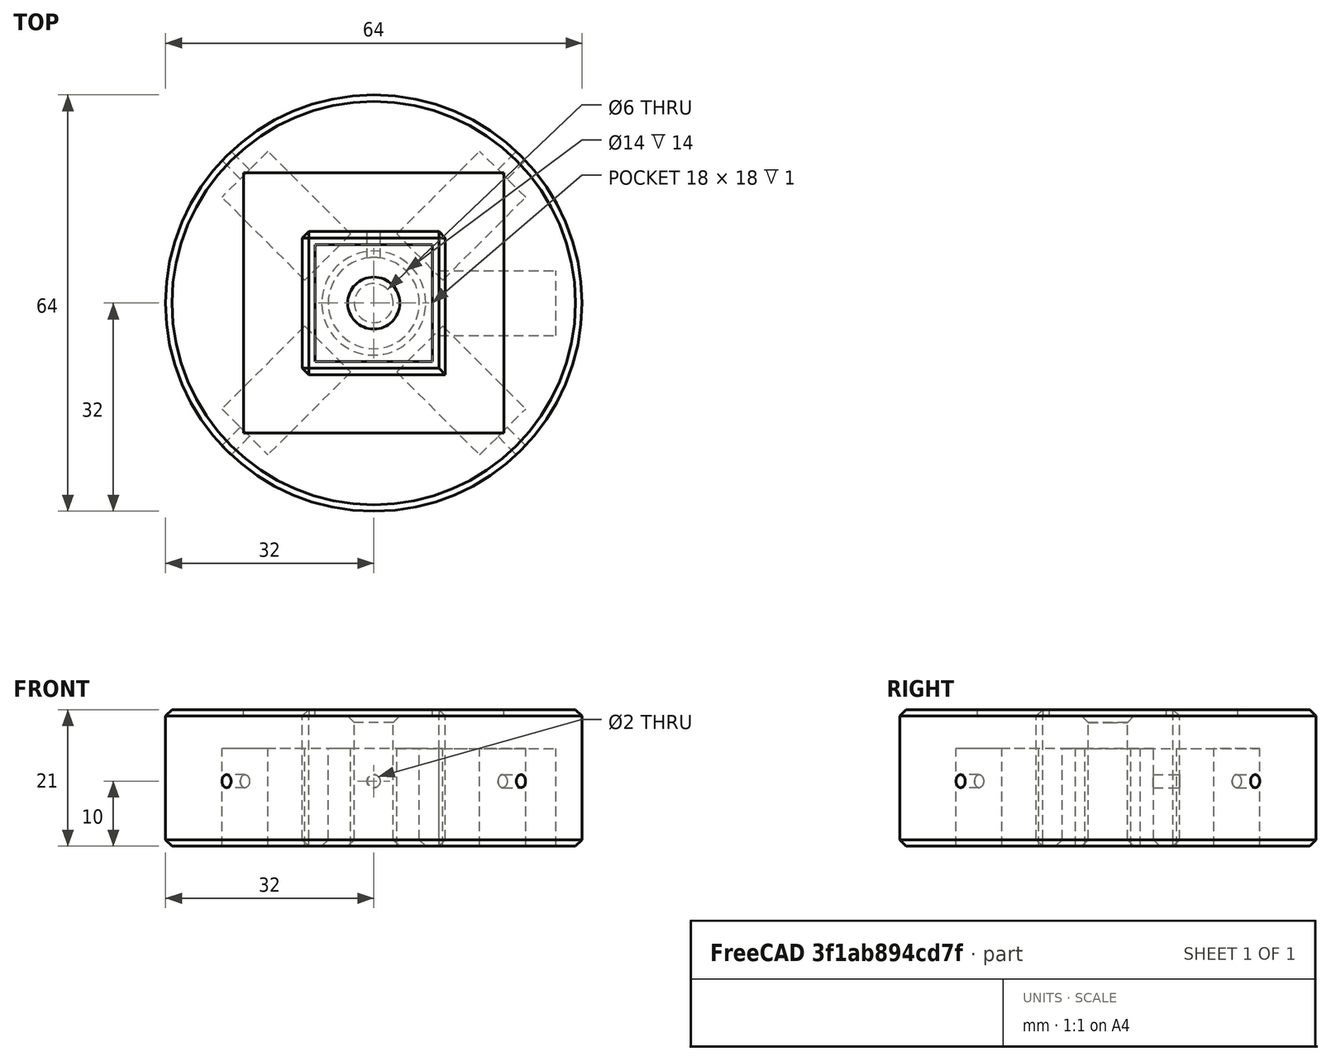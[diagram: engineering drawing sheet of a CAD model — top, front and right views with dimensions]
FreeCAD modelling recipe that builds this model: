
FCSTD DOCUMENT  (FreeCAD 0.18R16146 (Git))
Label: angle-drill-suporter
License: All rights reserved
LicenseURL: http://en.wikipedia.org/wiki/All_rights_reserved
objects: Part::Cylinder×8, Part::Cut×7, Part::Box×4, Part::Feature×4, Part::MultiFuse×2, Part::Chamfer×2
note: 27 computed .brp shape members not serialized (recipe doc carries the construction recipe); baked Part::Feature solids carry a one-line shape summary decoded from their .brp

FEATURE [Part::Cylinder] Cylinder
  Angle = 360
  AttacherType = Attacher::AttachEngine3D
  Height = 21
  Radius = 32
FEATURE [Part::Cylinder] Cylinder001
  Angle = 360
  AttacherType = Attacher::AttachEngine3D
  Height = 21
  Radius = 3
FEATURE [Part::Box] Box  label="Cube"
  AttacherType = Attacher::AttachEngine3D
  Height = 15
  Length = 18
  Placement = pos=(10,-5,0) rot=(0,0,1;0rad)
  Width = 10
FEATURE [Part::Feature] Box001  label="Cube001"
  Placement = pos=(0,0,0) rot=(0,0,1;0.785398rad)
  shape: bbox 19.8 x 19.8 x 15 mm, 6 faces (baked)
FEATURE [Part::Feature] Box002  label="Cube002"
  Placement = pos=(0,0,0) rot=(0,0,1;2.35619rad)
  shape: bbox 19.8 x 19.8 x 15 mm, 6 faces (baked)
FEATURE [Part::Feature] Box003  label="Cube003"
  Placement = pos=(0,0,0) rot=(0,0,1;3.92699rad)
  shape: bbox 19.8 x 19.8 x 15 mm, 6 faces (baked)
FEATURE [Part::Feature] Box004  label="Cube004"
  Placement = pos=(0,0,0) rot=(0,0,1;5.49779rad)
  shape: bbox 19.8 x 19.8 x 15 mm, 6 faces (baked)
FEATURE [Part::MultiFuse] Fusion
  Shapes = -> [Box004,Box001,Box002,Box003]
FEATURE [Part::Cut] Cut
  Base = -> Cylinder
  Tool = -> Cylinder001
FEATURE [Part::Cut] Cut001
  Base = -> Cut
  Tool = -> Fusion
FEATURE [Part::Box] Box005  label="Cube005"
  AttacherType = Attacher::AttachEngine3D
  Height = 10
  Length = 40
  Placement = pos=(-20,-20,20) rot=(0,0,1;0rad)
  Width = 40
FEATURE [Part::Cut] Cut002
  Base = -> Cut001
  Tool = -> Box005
FEATURE [Part::Cylinder] Cylinder002
  Angle = 360
  AttacherType = Attacher::AttachEngine3D
  Height = 40
  Placement = pos=(14.1421,14.1421,10) rot=(0.862856,-0.357407,0.357407;4.56541rad)
  Radius = 1
FEATURE [Part::Cylinder] Cylinder003
  Angle = 360
  AttacherType = Attacher::AttachEngine3D
  Height = 40
  Placement = pos=(14.1421,-14.1421,10) rot=(-0.281085,0.678598,-0.678598;2.59356rad)
  Radius = 1
FEATURE [Part::Cylinder] Cylinder004
  Angle = 360
  AttacherType = Attacher::AttachEngine3D
  Height = 40
  Placement = pos=(-14.1421,-14.1421,10) rot=(-0.281085,-0.678598,0.678598;2.59356rad)
  Radius = 1
FEATURE [Part::Cylinder] Cylinder005
  Angle = 360
  AttacherType = Attacher::AttachEngine3D
  Height = 40
  Placement = pos=(-14.1421,14.1421,10) rot=(-0.862856,-0.357407,0.357407;1.71777rad)
  Radius = 1
FEATURE [Part::MultiFuse] Fusion001
  Shapes = -> [Cylinder005,Cylinder003,Cylinder004,Cylinder002]
FEATURE [Part::Cut] Cut003
  Base = -> Cut002
  Tool = -> Fusion001
FEATURE [Part::Chamfer] Chamfer
  Base = -> Cut003
  Edges = 4 edges r=1: [Edge2,Edge3,Edge16,Edge53]
FEATURE [Part::Box] Box006  label="Cube006"
  AttacherType = Attacher::AttachEngine3D
  Height = 21
  Length = 22
  Width = 22
FEATURE [Part::Box] Box007  label="Cube007"
  AttacherType = Attacher::AttachEngine3D
  Height = 1
  Length = 18
  Placement = pos=(2,2,20) rot=(0,0,1;0rad)
  Width = 18
FEATURE [Part::Cut] Cut004
  Base = -> Box006
  Placement = pos=(-11,-11,0) rot=(0,0,1;0rad)
  Tool = -> Box007
FEATURE [Part::Cylinder] Cylinder006
  Angle = 360
  AttacherType = Attacher::AttachEngine3D
  Height = 15
  Radius = 7
FEATURE [Part::Cut] Cut005
  Base = -> Cut004
  Tool = -> Cylinder006
FEATURE [Part::Cylinder] Cylinder007
  Angle = 360
  AttacherType = Attacher::AttachEngine3D
  Height = 28
  Placement = pos=(0,2.2e-15,10) rot=(1,0,0;4.71239rad)
  Radius = 1
FEATURE [Part::Cut] Cut006
  Base = -> Cut005
  Tool = -> Cylinder007
FEATURE [Part::Chamfer] Chamfer001
  Base = -> Cut006
  Edges = 12 edges r=1: [Edge1,Edge2,Edge3,Edge4,Edge5,Edge7,Edge8,Edge9,Edge14,Edge15,Edge17,Edge18]
